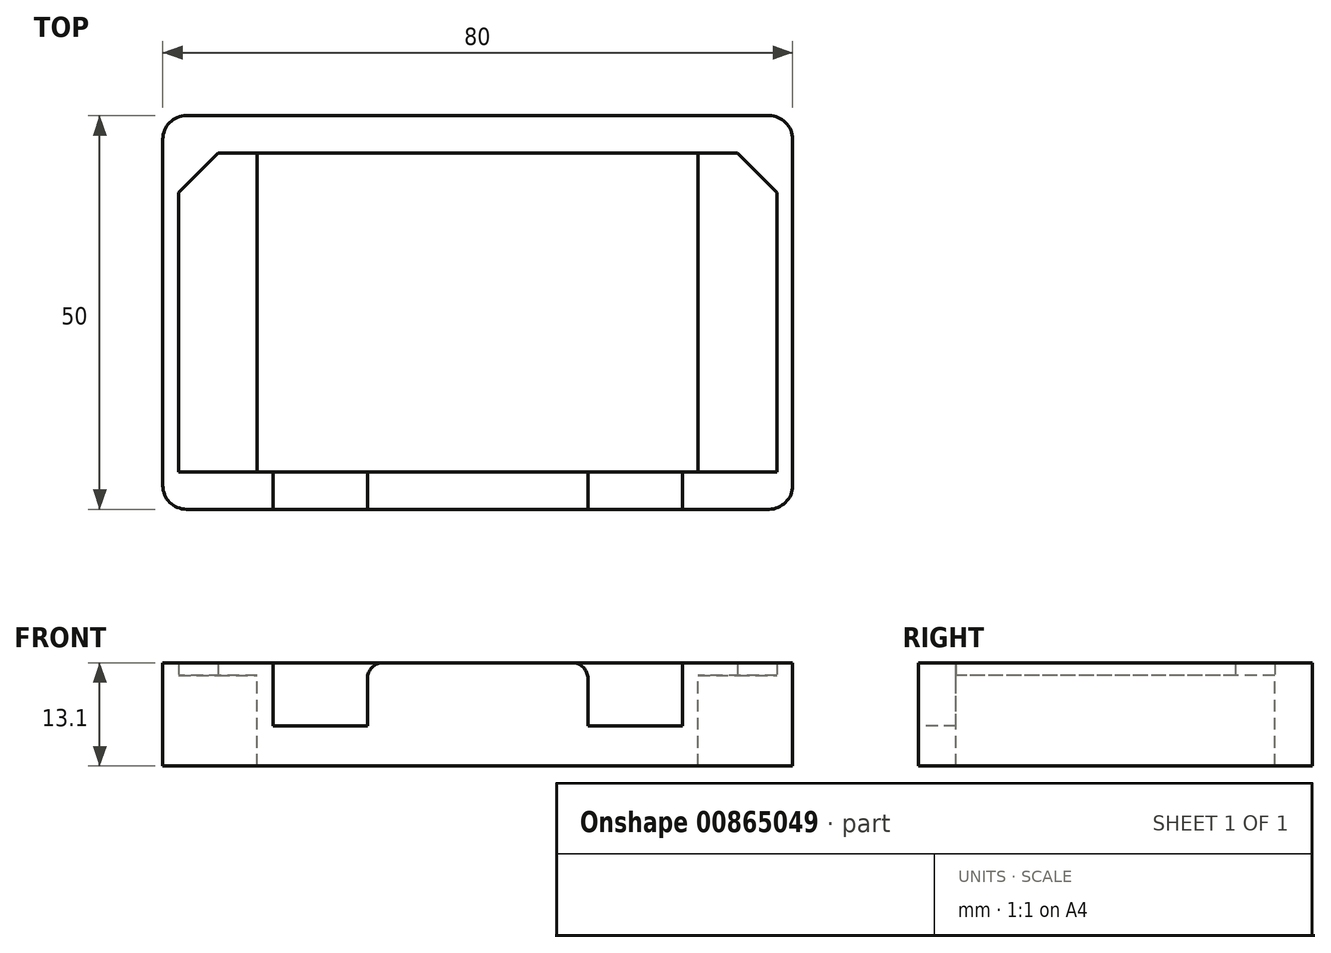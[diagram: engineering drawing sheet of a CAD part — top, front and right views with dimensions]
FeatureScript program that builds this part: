
annotation { "Feature Type Name" : "Feature", "Feature Type Description" : "" }
export const myFeature = defineFeature(function(context is Context, id is Id, definition is map)
    precondition{}
    {
        {
            var Q0;
            Q0=qCreatedBy(makeId("Top.planeOp"),FACE);
            var sketch = newSketch(context, id + "F0", { "sketchPlane" : qUnion([Q0])});
            skLineSegment(sketch, "E0.bottom", {"start": v(-40, 25) * mm, "end": v(40, 25) * mm});
            skLineSegment(sketch, "E0.top", {"start": v(-40, -25) * mm, "end": v(40, -25) * mm});
            skLineSegment(sketch, "E0.left", {"start": v(-40, 25) * mm, "end": v(-40, -25) * mm});
            skLineSegment(sketch, "E0.right", {"start": v(40, 25) * mm, "end": v(40, -25) * mm});
            skPoint(sketch, "E1", {"position": v(40, 0) * mm});
            skPoint(sketch, "E2", {"position": v(0, 25) * mm});
            skSolve(sketch);
        }
        {
            var Q0;
            Q0=makeQuery(id+"F0.imprint","IMPRINT",FACE,{"disambiguationData":[TD([[makeQuery(id+"F0.imprint","IMPRINT",EDGE,{"derivedFrom":sQuery(id+"F0.wireOp",EDGE,"E0.bottom")}),-1.0]])]});
            extrude(context, id + "F1", {"entities" : qUnion([Q0]), "oppositeDirection" : true, "depth" : 11.5 * mm, "offsetDistance" : 25 * mm});
        }
        {
            var Q0;
            Q0=makeQuery(id+"F1.opExtrude","CAP_FACE",FACE,{"disambiguationData":[OSD([sQuery(id+"F0.wireOp",EDGE,"E0.bottom"),sQuery(id+"F0.wireOp",EDGE,"E0.top"),sQuery(id+"F0.wireOp",EDGE,"E0.left"),sQuery(id+"F0.wireOp",EDGE,"E0.right")])],"isStart":true});
            var sketch = newSketch(context, id + "F2", { "sketchPlane" : qUnion([Q0])});
            skLineSegment(sketch, "E3.0.0", {"start": v(-40, 25) * mm, "end": v(-40, -25) * mm});
            skLineSegment(sketch, "E3.0.1", {"start": v(-40, -25) * mm, "end": v(40, -25) * mm});
            skLineSegment(sketch, "E3.0.2", {"start": v(40, -25) * mm, "end": v(40, 25) * mm});
            skLineSegment(sketch, "E3.0.3", {"start": v(40, 25) * mm, "end": v(-40, 25) * mm});
            skLineSegment(sketch, "E4", {"start": v(-38, -20.25) * mm, "end": v(-38, 15.25) * mm});
            skLineSegment(sketch, "E5", {"start": v(-38, 15.25) * mm, "end": v(-33, 20.25) * mm});
            skLineSegment(sketch, "E6", {"start": v(-33, 20.25) * mm, "end": v(33, 20.25) * mm});
            skLineSegment(sketch, "E7", {"start": v(33, 20.25) * mm, "end": v(38, 15.25) * mm});
            skLineSegment(sketch, "E8", {"start": v(38, 15.25) * mm, "end": v(38, -20.25) * mm});
            skLineSegment(sketch, "E9", {"start": v(38, -20.25) * mm, "end": v(-38, -20.25) * mm});
            skPoint(sketch, "E10", {"position": v(0, 20.25) * mm});
            skLineSegment(sketch, "E11", {"start": v(0, 20.25) * mm, "end": v(0, 25) * mm, "construction": true});
            skPoint(sketch, "E12", {"position": v(0, -20.25) * mm});
            skLineSegment(sketch, "E13", {"start": v(0, -20.25) * mm, "end": v(0, -25) * mm, "construction": true});
            skSolve(sketch);
        }
        {
            var Q0;
            Q0=makeQuery(id+"F2.imprint","IMPRINT",FACE,{"disambiguationData":[TD([[makeQuery(id+"F2.imprint","IMPRINT",EDGE,{"derivedFrom":sQuery(id+"F2.wireOp",EDGE,"E3.0.0")}),1.0]])]});
            extrude(context, id + "F3", {"entities" : qUnion([Q0]), "operationType" : NewBodyOperationType.ADD, "depth" : 1.6 * mm, "offsetDistance" : 25 * mm});
        }
        {
            var Q0;
            Q0=makeQuery(id+"F1.opExtrude","CAP_FACE",FACE,{"disambiguationData":[OSD([sQuery(id+"F0.wireOp",EDGE,"E0.bottom"),sQuery(id+"F0.wireOp",EDGE,"E0.top"),sQuery(id+"F0.wireOp",EDGE,"E0.left"),sQuery(id+"F0.wireOp",EDGE,"E0.right")])],"isStart":true});
            var sketch = newSketch(context, id + "F4", { "sketchPlane" : qUnion([Q0])});
            skLineSegment(sketch, "E14.bottom", {"start": v(-28, 20.25) * mm, "end": v(28, 20.25) * mm});
            skLineSegment(sketch, "E14.top", {"start": v(-28, -20.25) * mm, "end": v(28, -20.25) * mm});
            skLineSegment(sketch, "E14.left", {"start": v(-28, 20.25) * mm, "end": v(-28, -20.25) * mm});
            skLineSegment(sketch, "E14.right", {"start": v(28, 20.25) * mm, "end": v(28, -20.25) * mm});
            skPoint(sketch, "E15", {"position": v(0, 20.25) * mm});
            skSolve(sketch);
        }
        {
            var Q0;
            Q0=makeQuery(id+"F4.imprint","IMPRINT",FACE,{"disambiguationData":[TD([[makeQuery(id+"F4.imprint","IMPRINT",EDGE,{"derivedFrom":sQuery(id+"F4.wireOp",EDGE,"E14.bottom")}),-1.0]])]});
            extrude(context, id + "F5", {"entities" : qUnion([Q0]), "operationType" : NewBodyOperationType.REMOVE, "endBound" : BoundingType.UP_TO_NEXT, "oppositeDirection" : true, "depth" : 25 * mm, "offsetDistance" : 25 * mm});
        }
        {
            var Q0;
            Q0=makeQuery(id+"F3.opExtrude","CAP_FACE",FACE,{"disambiguationData":[OSD([sQuery(id+"F2.wireOp",EDGE,"E3.0.0"),sQuery(id+"F2.wireOp",EDGE,"E3.0.1"),sQuery(id+"F2.wireOp",EDGE,"E3.0.2"),sQuery(id+"F2.wireOp",EDGE,"E3.0.3"),sQuery(id+"F2.wireOp",EDGE,"E4"),sQuery(id+"F2.wireOp",EDGE,"E5"),sQuery(id+"F2.wireOp",EDGE,"E6"),sQuery(id+"F2.wireOp",EDGE,"E7"),sQuery(id+"F2.wireOp",EDGE,"E8"),sQuery(id+"F2.wireOp",EDGE,"E9")])],"isStart":false});
            var sketch = newSketch(context, id + "F6", { "sketchPlane" : qUnion([Q0])});
            skLineSegment(sketch, "E16.bottom", {"start": v(-26, -20.25) * mm, "end": v(-14, -20.25) * mm});
            skLineSegment(sketch, "E16.top", {"start": v(-26, -25) * mm, "end": v(-14, -25) * mm});
            skLineSegment(sketch, "E16.left", {"start": v(-26, -20.25) * mm, "end": v(-26, -25) * mm});
            skLineSegment(sketch, "E16.right", {"start": v(-14, -20.25) * mm, "end": v(-14, -25) * mm});
            skLineSegment(sketch, "E17.bottom", {"start": v(14, -20.25) * mm, "end": v(26, -20.25) * mm});
            skLineSegment(sketch, "E17.top", {"start": v(14, -25) * mm, "end": v(26, -25) * mm});
            skLineSegment(sketch, "E17.left", {"start": v(14, -20.25) * mm, "end": v(14, -25) * mm});
            skLineSegment(sketch, "E17.right", {"start": v(26, -20.25) * mm, "end": v(26, -25) * mm});
            skLineSegment(sketch, "E18", {"start": v(-14, -20.25) * mm, "end": v(14, -20.25) * mm, "construction": true});
            skPoint(sketch, "E19", {"position": v(0, -20.25) * mm});
            skSolve(sketch);
        }
        {
            var Q0;
            Q0=makeQuery(id+"F6.imprint","IMPRINT",FACE,{"disambiguationData":[TD([[makeQuery(id+"F6.imprint","IMPRINT",EDGE,{"derivedFrom":sQuery(id+"F6.wireOp",EDGE,"E16.bottom")}),1.0]])]});
            var Q1;
            Q1=makeQuery(id+"F6.imprint","IMPRINT",FACE,{"disambiguationData":[TD([[makeQuery(id+"F6.imprint","IMPRINT",EDGE,{"derivedFrom":sQuery(id+"F6.wireOp",EDGE,"E17.bottom")}),1.0]])]});
            extrude(context, id + "F7", {"entities" : qUnion([Q0, Q1]), "operationType" : NewBodyOperationType.REMOVE, "oppositeDirection" : true, "depth" : 8 * mm, "offsetDistance" : 25 * mm});
        }
        {
            var Q0;
            Q0=makeQuery(id+"F3.boolean.opBoolean","MERGE",EDGE,{"derivedFrom":[makeQuery(id+"F1.opExtrude","SWEPT_EDGE",EDGE,{"disambiguationData":[OSD([sQuery(id+"F0.wireOp",EDGE,"E0.bottom"),sQuery(id+"F0.wireOp",EDGE,"E0.left")])]}),makeQuery(id+"F3.opExtrude","SWEPT_EDGE",EDGE,{"disambiguationData":[OSD([sQuery(id+"F2.wireOp",EDGE,"E3.0.0"),sQuery(id+"F2.wireOp",EDGE,"E3.0.3")])]})]});
            var Q1;
            Q1=makeQuery(id+"F3.boolean.opBoolean","MERGE",EDGE,{"derivedFrom":[makeQuery(id+"F1.opExtrude","SWEPT_EDGE",EDGE,{"disambiguationData":[OSD([sQuery(id+"F0.wireOp",EDGE,"E0.top"),sQuery(id+"F0.wireOp",EDGE,"E0.left")])]}),makeQuery(id+"F3.opExtrude","SWEPT_EDGE",EDGE,{"disambiguationData":[OSD([sQuery(id+"F2.wireOp",EDGE,"E3.0.0"),sQuery(id+"F2.wireOp",EDGE,"E3.0.1")])]})]});
            var Q2;
            Q2=makeQuery(id+"F3.boolean.opBoolean","MERGE",EDGE,{"derivedFrom":[makeQuery(id+"F1.opExtrude","SWEPT_EDGE",EDGE,{"disambiguationData":[OSD([sQuery(id+"F0.wireOp",EDGE,"E0.top"),sQuery(id+"F0.wireOp",EDGE,"E0.right")])]}),makeQuery(id+"F3.opExtrude","SWEPT_EDGE",EDGE,{"disambiguationData":[OSD([sQuery(id+"F2.wireOp",EDGE,"E3.0.1"),sQuery(id+"F2.wireOp",EDGE,"E3.0.2")])]})]});
            var Q3;
            Q3=makeQuery(id+"F3.boolean.opBoolean","MERGE",EDGE,{"derivedFrom":[makeQuery(id+"F1.opExtrude","SWEPT_EDGE",EDGE,{"disambiguationData":[OSD([sQuery(id+"F0.wireOp",EDGE,"E0.bottom"),sQuery(id+"F0.wireOp",EDGE,"E0.right")])]}),makeQuery(id+"F3.opExtrude","SWEPT_EDGE",EDGE,{"disambiguationData":[OSD([sQuery(id+"F2.wireOp",EDGE,"E3.0.2"),sQuery(id+"F2.wireOp",EDGE,"E3.0.3")])]})]});
            fillet(context, id + "F8", {"entities" : qUnion([Q0, Q1, Q2, Q3]), "radius" : 3 * mm, "tangentPropagation" : true, "allowEdgeOverflow" : false});
        }
        {
            var Q0;
            Q0=makeQuery(id+"F7.boolean.opBoolean","COPY",EDGE,{"derivedFrom":makeQuery(id+"F7.opExtrude","CAP_EDGE",EDGE,{"disambiguationData":[OSD([sQuery(id+"F6.wireOp",EDGE,"E16.left")])],"isStart":true})});
            var Q1;
            Q1=makeQuery(id+"F7.boolean.opBoolean","COPY",EDGE,{"derivedFrom":makeQuery(id+"F7.opExtrude","CAP_EDGE",EDGE,{"disambiguationData":[OSD([sQuery(id+"F6.wireOp",EDGE,"E16.right")])],"isStart":true})});
            var Q2;
            Q2=makeQuery(id+"F7.boolean.opBoolean","COPY",EDGE,{"derivedFrom":makeQuery(id+"F7.opExtrude","CAP_EDGE",EDGE,{"disambiguationData":[OSD([sQuery(id+"F6.wireOp",EDGE,"E17.left")])],"isStart":true})});
            var Q3;
            Q3=makeQuery(id+"F7.boolean.opBoolean","COPY",EDGE,{"derivedFrom":makeQuery(id+"F7.opExtrude","CAP_EDGE",EDGE,{"disambiguationData":[OSD([sQuery(id+"F6.wireOp",EDGE,"E17.right")])],"isStart":true})});
            fillet(context, id + "F9", {"entities" : qUnion([Q0, Q1, Q2, Q3]), "radius" : 2 * mm, "tangentPropagation" : true, "allowEdgeOverflow" : false});
        }
    });
